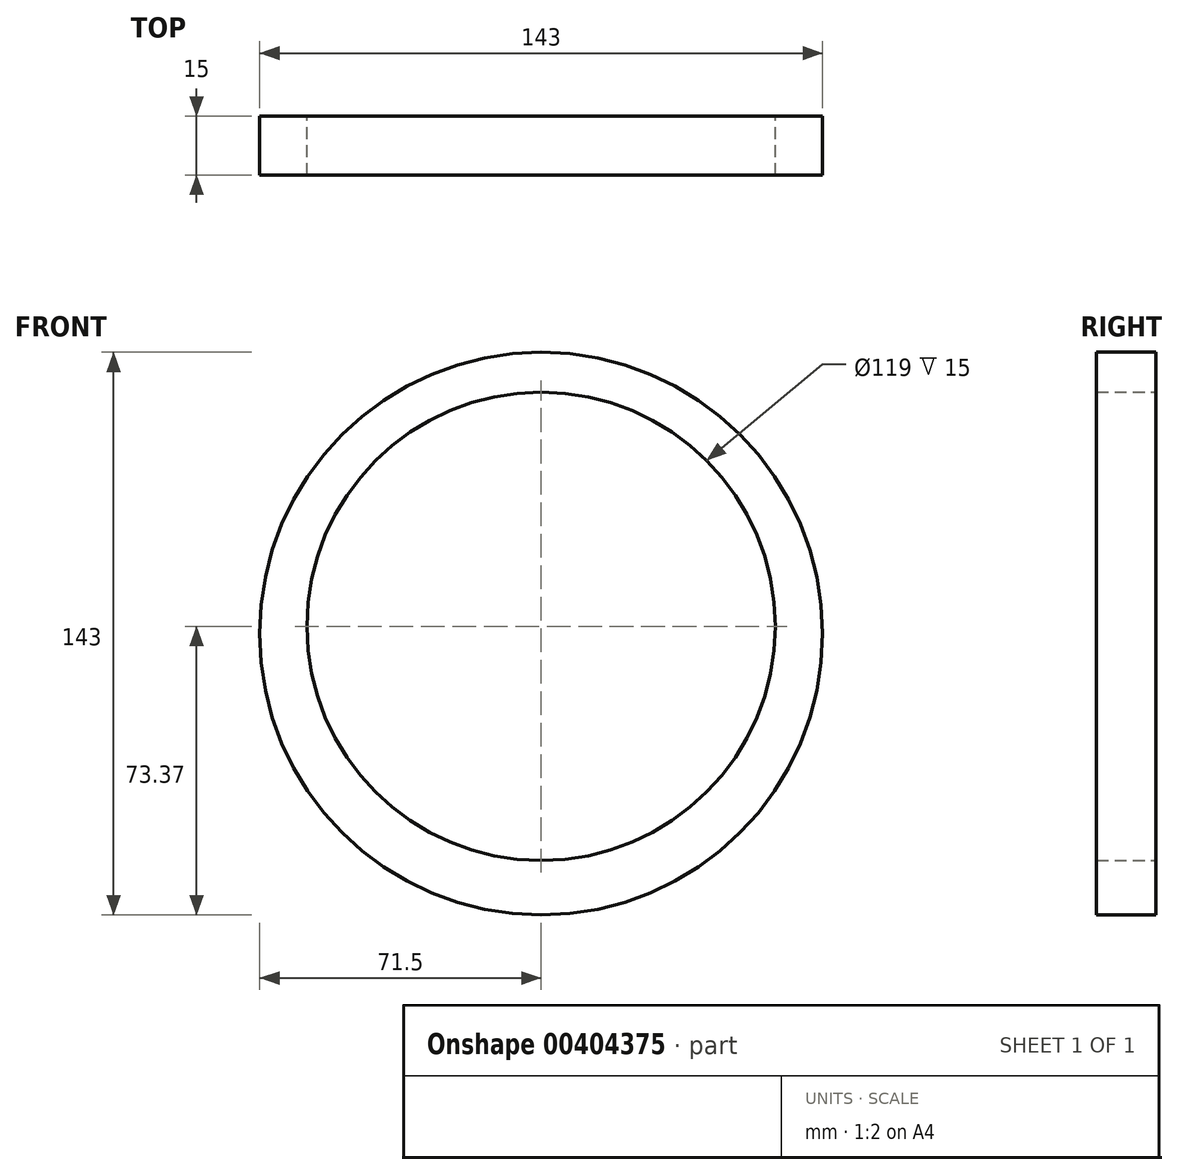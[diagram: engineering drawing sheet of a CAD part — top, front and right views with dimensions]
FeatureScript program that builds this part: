
annotation { "Feature Type Name" : "Feature", "Feature Type Description" : "" }
export const myFeature = defineFeature(function(context is Context, id is Id, definition is map)
    precondition{}
    {
        {
            var Q0;
            Q0=qCreatedBy(makeId("Front.planeOp"),FACE);
            var sketch = newSketch(context, id + "F0", { "sketchPlane" : qUnion([Q0])});
            skCircle(sketch, "E0", {"center": v(0, 0) * mm, "radius": 59.5 * mm});
            skCircle(sketch, "E1", {"center": v(0, -1.87) * mm, "radius": 71.5 * mm});
            skSolve(sketch);
        }
        {
            var Q0;
            Q0 = qSketchRegion(id + "F0", true);
            extrude(context, id + "F1", {"entities" : qUnion([Q0]), "depth" : 15 * mm});
        }
    });
